# Revit family: IS_Altes_R0130_BIM_DE
name_source: partatom
category: Plumbing Fixtures
revit_build: Autodesk Revit 2017 (Build: 20160225_1515(x64)
units: mm (PartAtom-declared; Revit-internal decimal feet)

## family parameters
Cut with Voids When Loaded = No
Host = Face
OmniClass Number = 23.45.05.21.11.11
OmniClass Title = Water Operated Water Closets
Part Type = Normal
Room Calculation Point = No
Round Connector Dimension = Use Diameter
Shared = Yes

## types (2) — shared parameters
AfstandsEenheid = millimeters
Artikelreferentie = 1
Assembly Code = C1030200
Auteur = Ideal Standrad
BREEAMApproved = No
Beschrijvinggarantie = Manufacturers Warranty
Default Elevation = 900 mm  [stored 2.95276 ft]
Douchebak = No
DuurEenheid = year
ECA = No
Garantieunits = Year
Heefthandvaten = No
Hulp = https://www.idealstandard.de
Installatieinstructies = https://www.idealstandard.de
Materiaal = Metal
Merk = Ideal Standard
Montageinstuctie = https://www.idealstandard.de
NBSDescription = WC cistern fittings
NBSReference = 45-30-70/387
Nettogewicht = 5.7915
Productinformatie = https://www.idealstandard.de
Telefoonnummer = +49 (0) 6571 16 0
URL = https://www.idealstandard.de
Uniclass2 = Pr_40_20_93_89
Uniclass2015Description = Urinal and WC fittings
Uniclass2015Referentie = Pr_40_20_93
Urlproducent = https://www.idealstandard.de
Versie = 1
Verwachtelevensduur = 5
Volumeunits = Litres
WRAS = No
WaterEfficientProduct = No
zero-valued in all types: Breedte, BrutoGewicht, CWFU, Cost, Diepte, GrootteAfvoergat, HWFU, Lengte, Overloop, Vervangingskosten, WFU

## per-type parameters (varying)
| type | Afmetingen | Afwerking | Artikelnummer | Artikelomschrijving | Barcode | BimObjectNaam | Description | Flush Plate Material | Kleur | Model |
| R0130AC - ALTES NT WHITE - ISI | 234 x 12 x 157mm | White | R0130AC | Sensor-Betätigungsplatte NT1 ALTES, Schwarz | 3391500580565 | IS_Ideal Standard_WC cistern fittings_Altes_R0130AC | New 7 Ceramic Soft Square button Sensor plate, White - DF | IS_White | White | R0130AC |
| R0130A6 - ALTES NT BLACK - ISI | 220 x 4 x 150mm | Black | R0130A6 | Betätigungsplatte M1 OLEAS, mechanischen Auslösung, Weiß | 3391500580558 | IS_Ideal Standard_WC cistern fittings_Altes_R0130A6 | New 7 Ceramic Soft Square button Sensor plate, Black - DF | IS_Black | Black | R0130A6 |

note: [stored X ft] marks values corroborated as IEEE doubles in the binary element streams (Revit-internal decimal feet)

## geometry (parser evidence)
native form markers: Sweep x1
no freeform markers — native parametric forms only
